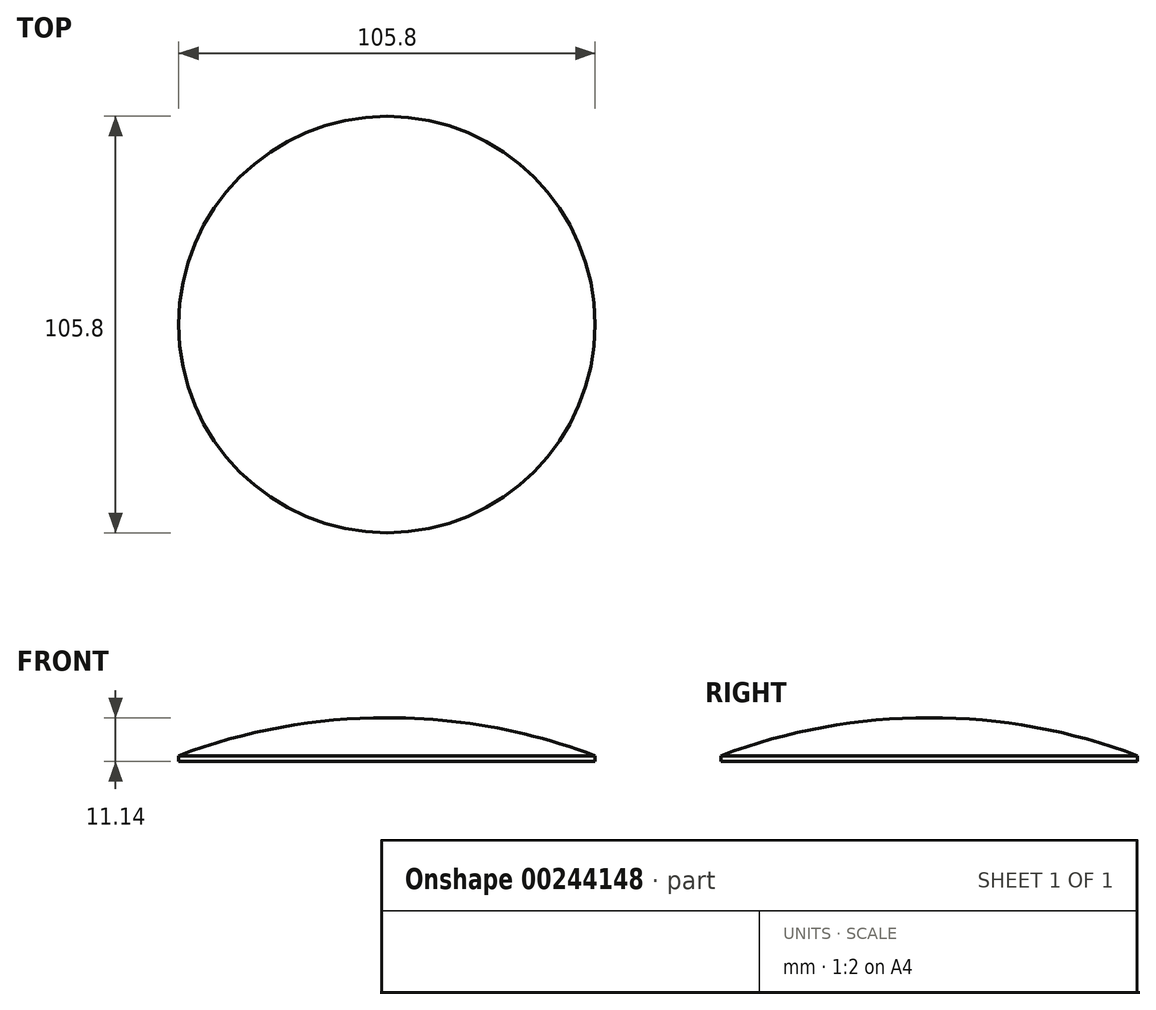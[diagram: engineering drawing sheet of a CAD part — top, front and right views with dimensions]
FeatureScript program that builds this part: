
annotation { "Feature Type Name" : "Feature", "Feature Type Description" : "" }
export const myFeature = defineFeature(function(context is Context, id is Id, definition is map)
    precondition{}
    {
        {
            var Q0;
            Q0=qCreatedBy(makeId("Front.planeOp"),FACE);
            var sketch = newSketch(context, id + "F0", { "sketchPlane" : qUnion([Q0])});
            skLineSegment(sketch, "E0", {"start": v(0, 0) * mm, "end": v(0, -150.02) * mm, "construction": true});
            skArc(sketch, "E1", {"start": v(52.9, -9.64) * mm, "mid": v(26.89, -2.43) * mm, "end": v(0, 0) * mm});
            skLineSegment(sketch, "E2", {"start": v(0, 0) * mm, "end": v(52.9, 0) * mm, "construction": true});
            skLineSegment(sketch, "E3", {"start": v(52.9, 0) * mm, "end": v(52.9, -9.64) * mm, "construction": true});
            skLineSegment(sketch, "E4", {"start": v(52.9, -9.64) * mm, "end": v(0, -9.64) * mm, "construction": true});
            skLineSegment(sketch, "E5", {"start": v(52.9, -9.64) * mm, "end": v(52.9, -11.14) * mm});
            skLineSegment(sketch, "E6", {"start": v(52.9, -11.14) * mm, "end": v(0, -11.14) * mm});
            skLineSegment(sketch, "E7", {"start": v(0, -11.14) * mm, "end": v(0, 0) * mm});
            skLineSegment(sketch, "E8.MirrorCS", {"start": v(0, -22.27) * mm, "end": v(0, 127.75) * mm, "construction": true});
            skLineSegment(sketch, "E9", {"start": v(111.82, -23.58) * mm, "end": v(136.82, -23.58) * mm});
            skLineSegment(sketch, "E10", {"start": v(111.82, -23.58) * mm, "end": v(111.82, 26.42) * mm});
            skLineSegment(sketch, "E11.MirrorCS", {"start": v(111.82, -23.58) * mm, "end": v(86.82, -23.58) * mm});
            skSolve(sketch);
        }
        {
            var Q0;
            Q0 = qSketchRegion(id + "F0", true);
            var Q1;
            Q1=sQuery(id+"F0.wireOp",EDGE,"E7");
            revolve(context, id + "F1", {"entities" : qUnion([Q0]), "axis" : qUnion([Q1]), "revolveType" : RevolveType.FULL});
        }
    });
